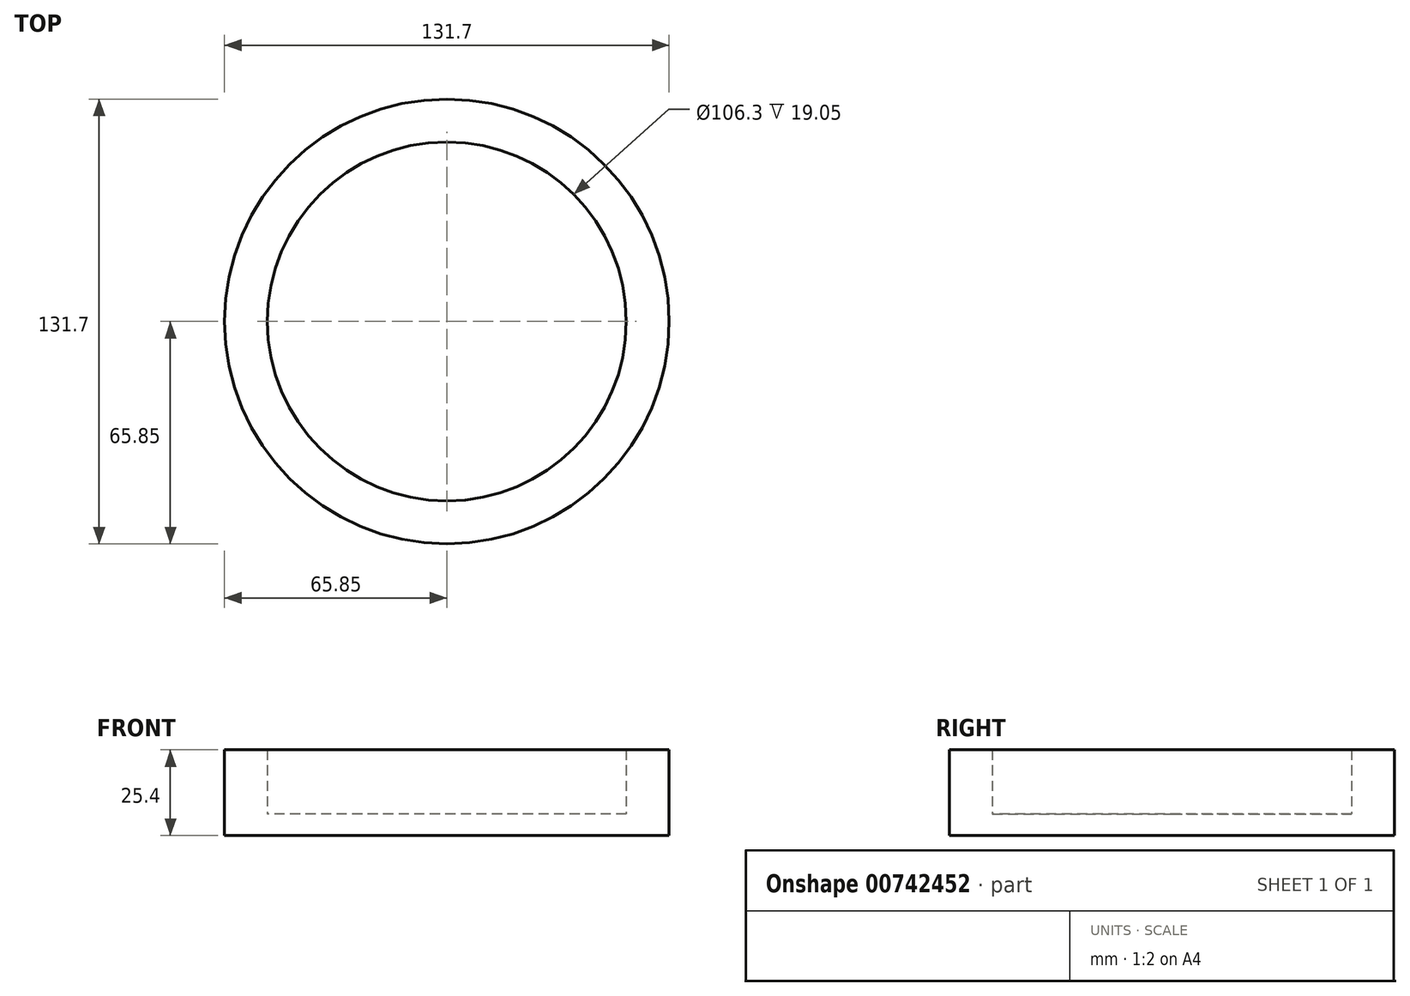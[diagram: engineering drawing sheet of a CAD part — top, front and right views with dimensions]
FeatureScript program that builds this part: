
annotation { "Feature Type Name" : "Feature", "Feature Type Description" : "" }
export const myFeature = defineFeature(function(context is Context, id is Id, definition is map)
    precondition{}
    {
        {
            var Q0;
            Q0=qCreatedBy(makeId("Top.planeOp"),FACE);
            var sketch = newSketch(context, id + "F0", { "sketchPlane" : qUnion([Q0])});
            skCircle(sketch, "E0", {"center": v(0, 0) * mm, "radius": 65.85 * mm});
            skCircle(sketch, "E1.0", {"center": v(0, 0) * mm, "radius": 53.15 * mm});
            skSolve(sketch);
        }
        {
            var Q0;
            Q0=makeQuery(id+"F0.imprint","IMPRINT",FACE,{"disambiguationData":[TD([[makeQuery(id+"F0.imprint","IMPRINT",EDGE,{"derivedFrom":sQuery(id+"F0.wireOp",EDGE,"E0")}),1.0]])]});
            extrude(context, id + "F1", {"entities" : qUnion([Q0]), "depth" : 25.4 * mm, "offsetDistance" : 25.4 * mm});
        }
        {
            var Q0;
            Q0=qCreatedBy(makeId("Top.planeOp"),FACE);
            var sketch = newSketch(context, id + "F2", { "sketchPlane" : qUnion([Q0])});
            skCircle(sketch, "E2", {"center": v(0, 0) * mm, "radius": 53.15 * mm});
            skSolve(sketch);
        }
        {
            var Q0;
            Q0=makeQuery(id+"F2.imprint","IMPRINT",FACE,{"disambiguationData":[TD([[makeQuery(id+"F2.imprint","IMPRINT",EDGE,{"derivedFrom":sQuery(id+"F2.wireOp",EDGE,"E2")}),1.0]])]});
            extrude(context, id + "F3", {"entities" : qUnion([Q0]), "operationType" : NewBodyOperationType.ADD, "depth" : 6.35 * mm, "offsetDistance" : 25.4 * mm});
        }
    });
